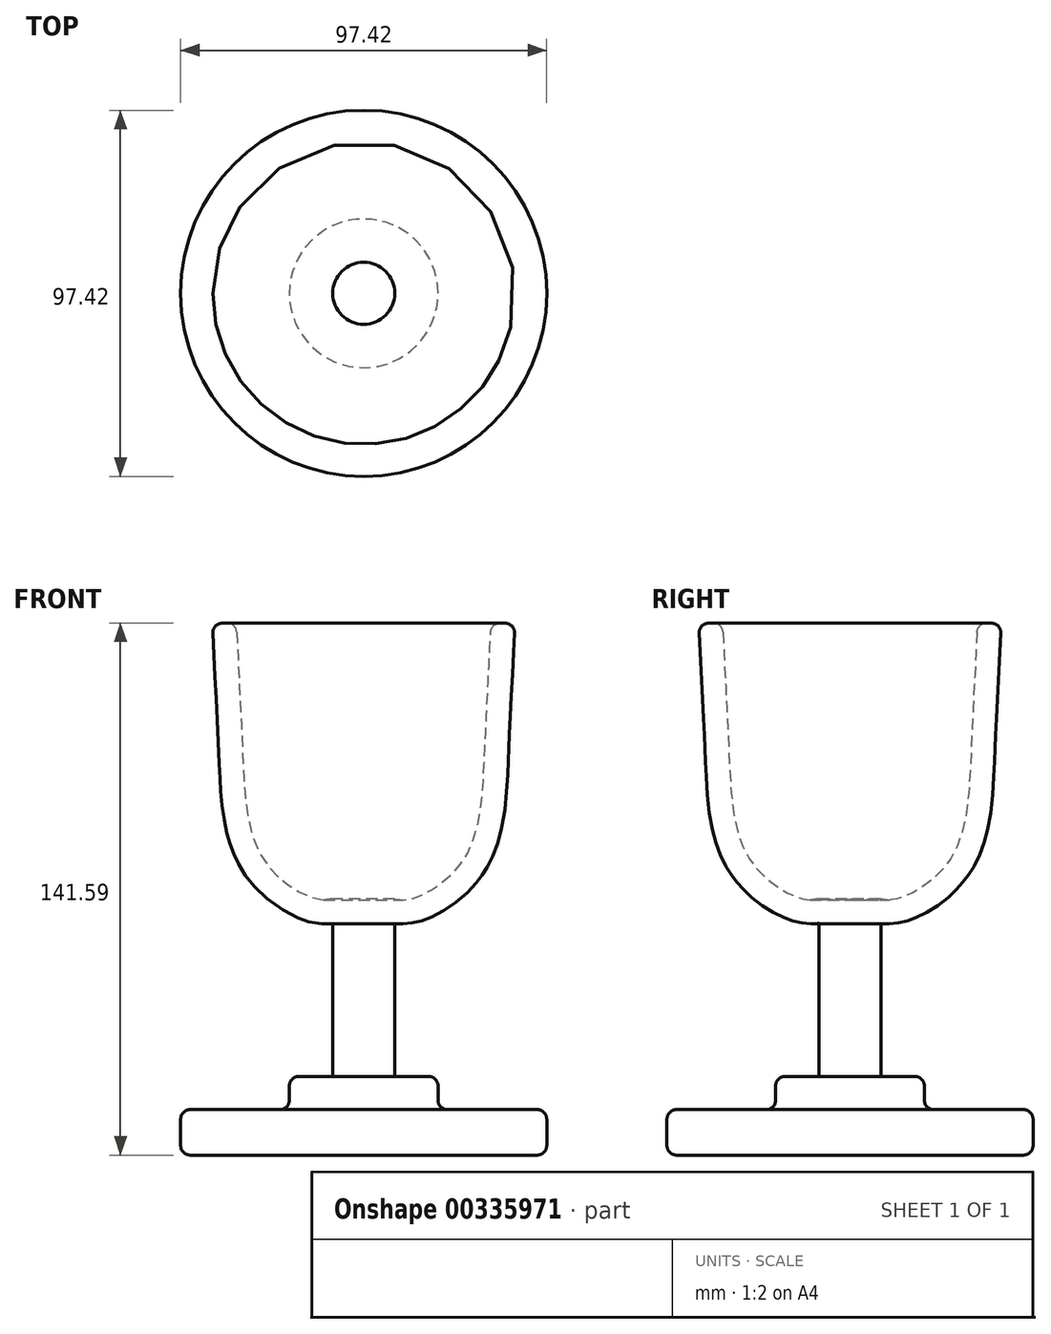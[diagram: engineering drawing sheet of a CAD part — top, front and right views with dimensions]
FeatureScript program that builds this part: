
annotation { "Feature Type Name" : "Feature", "Feature Type Description" : "" }
export const myFeature = defineFeature(function(context is Context, id is Id, definition is map)
    precondition{}
    {
        {
            var Q0;
            Q0=qCreatedBy(makeId("Front.planeOp"),FACE);
            var sketch = newSketch(context, id + "F0", { "sketchPlane" : qUnion([Q0])});
            skLineSegment(sketch, "E0", {"start": v(0, 0) * mm, "end": v(48.71, 0) * mm});
            skLineSegment(sketch, "E1", {"start": v(48.71, 0) * mm, "end": v(48.71, 12.1) * mm});
            skLineSegment(sketch, "E2", {"start": v(48.71, 12.1) * mm, "end": v(19.78, 12.1) * mm});
            skLineSegment(sketch, "E3", {"start": v(19.78, 12.1) * mm, "end": v(19.78, 20.96) * mm});
            skLineSegment(sketch, "E4", {"start": v(19.78, 20.96) * mm, "end": v(8.27, 20.96) * mm});
            skLineSegment(sketch, "E5", {"start": v(8.27, 20.96) * mm, "end": v(8.27, 61.75) * mm});
            skFitSpline(sketch, "E6", {"points": [v(8.27, 68.2) * mm, v(12.7, 68.2) * mm, v(26.57, 78.53) * mm, v(32.18, 106.29) * mm, v(33.95, 141.72) * mm], "startDerivative": vector(31.4, -6.02) * mm, "endDerivative": vector(5.5, 105.12) * mm});
            skFitSpline(sketch, "E7.0", {"points": [v(7.07, 61.96) * mm, v(7.4, 61.9) * mm, v(8.24, 61.74) * mm, v(9.76, 61.57) * mm, v(11.16, 61.57) * mm, v(12.28, 61.66) * mm, v(13.44, 61.84) * mm, v(14.63, 62.13) * mm, v(15.8, 62.5) * mm, v(17.35, 63.07) * mm, v(19.33, 63.98) * mm, v(21.75, 65.35) * mm, v(24.19, 67) * mm, v(26.6, 68.95) * mm, v(28.53, 70.82) * mm, v(29.99, 72.48) * mm, v(30.86, 73.6) * mm, v(31.53, 74.52) * mm, v(32.17, 75.48) * mm, v(32.91, 76.7) * mm, v(33.7, 78.21) * mm, v(34.64, 80.26) * mm, v(35.6, 82.87) * mm, v(36.48, 86.06) * mm, v(37.35, 90.37) * mm, v(37.86, 94.73) * mm, v(38.18, 99.09) * mm, v(38.36, 102.34) * mm, v(38.48, 105.04) * mm, v(38.58, 107.17) * mm, v(38.68, 109.31) * mm, v(38.8, 112) * mm, v(39, 116.3) * mm, v(39.28, 121.73) * mm, v(39.6, 128.26) * mm, v(39.95, 134.81) * mm, v(40.18, 139.2) * mm, v(40.3, 141.38) * mm]});
            skLineSegment(sketch, "E8", {"start": v(33.95, 141.72) * mm, "end": v(40.3, 141.38) * mm});
            skLineSegment(sketch, "E9", {"start": v(0, 68.2) * mm, "end": v(0, 0) * mm});
            skLineSegment(sketch, "E10.trimOffspring", {"start": v(8.27, 68) * mm, "end": v(8.27, 68.2) * mm});
            skLineSegment(sketch, "E11", {"start": v(8.27, 68.2) * mm, "end": v(0, 68.2) * mm});
            skSolve(sketch);
        }
        {
            var Q0;
            Q0=makeQuery(id+"F0.imprint","IMPRINT",FACE,{"disambiguationData":[TD([[makeQuery(id+"F0.imprint","IMPRINT",EDGE,{"derivedFrom":sQuery(id+"F0.wireOp",EDGE,"E0")}),1.0]])]});
            var Q1;
            Q1=sQuery(id+"F0.wireOp",EDGE,"E9");
            revolve(context, id + "F1", {"entities" : qUnion([Q0]), "axis" : qUnion([Q1]), "revolveType" : RevolveType.FULL});
        }
        {
            var Q0;
            Q0=makeQuery(id+"F1.opRevolve","SWEPT_EDGE",EDGE,{"disambiguationData":[OSD([sQuery(id+"F0.wireOp",EDGE,"E3"),sQuery(id+"F0.wireOp",EDGE,"E4")])]});
            var Q1;
            Q1=makeQuery(id+"F1.opRevolve","SWEPT_EDGE",EDGE,{"disambiguationData":[OSD([sQuery(id+"F0.wireOp",EDGE,"E1"),sQuery(id+"F0.wireOp",EDGE,"E2")])]});
            var Q2;
            Q2=makeQuery(id+"F1.opRevolve","SWEPT_EDGE",EDGE,{"disambiguationData":[OSD([sQuery(id+"F0.wireOp",EDGE,"E6"),sQuery(id+"F0.wireOp",EDGE,"E8")])]});
            var Q3;
            Q3=makeQuery(id+"F1.opRevolve","SWEPT_EDGE",EDGE,{"disambiguationData":[OSD([sQuery(id+"F0.wireOp",EDGE,"E2"),sQuery(id+"F0.wireOp",EDGE,"E3")])]});
            var Q4;
            Q4=makeQuery(id+"F1.opRevolve","SWEPT_EDGE",EDGE,{"disambiguationData":[OSD([sQuery(id+"F0.wireOp",EDGE,"E0"),sQuery(id+"F0.wireOp",EDGE,"E1")])]});
            var Q5;
            Q5=makeQuery(id+"F1.opRevolve","SWEPT_EDGE",EDGE,{"disambiguationData":[OSD([sQuery(id+"F0.wireOp",EDGE,"E7.0"),sQuery(id+"F0.wireOp",EDGE,"E8")])]});
            fillet(context, id + "F2", {"entities" : qUnion([Q0, Q1, Q2, Q3, Q4, Q5]), "radius" : 2.54 * mm, "tangentPropagation" : true, "allowEdgeOverflow" : false});
        }
    });
